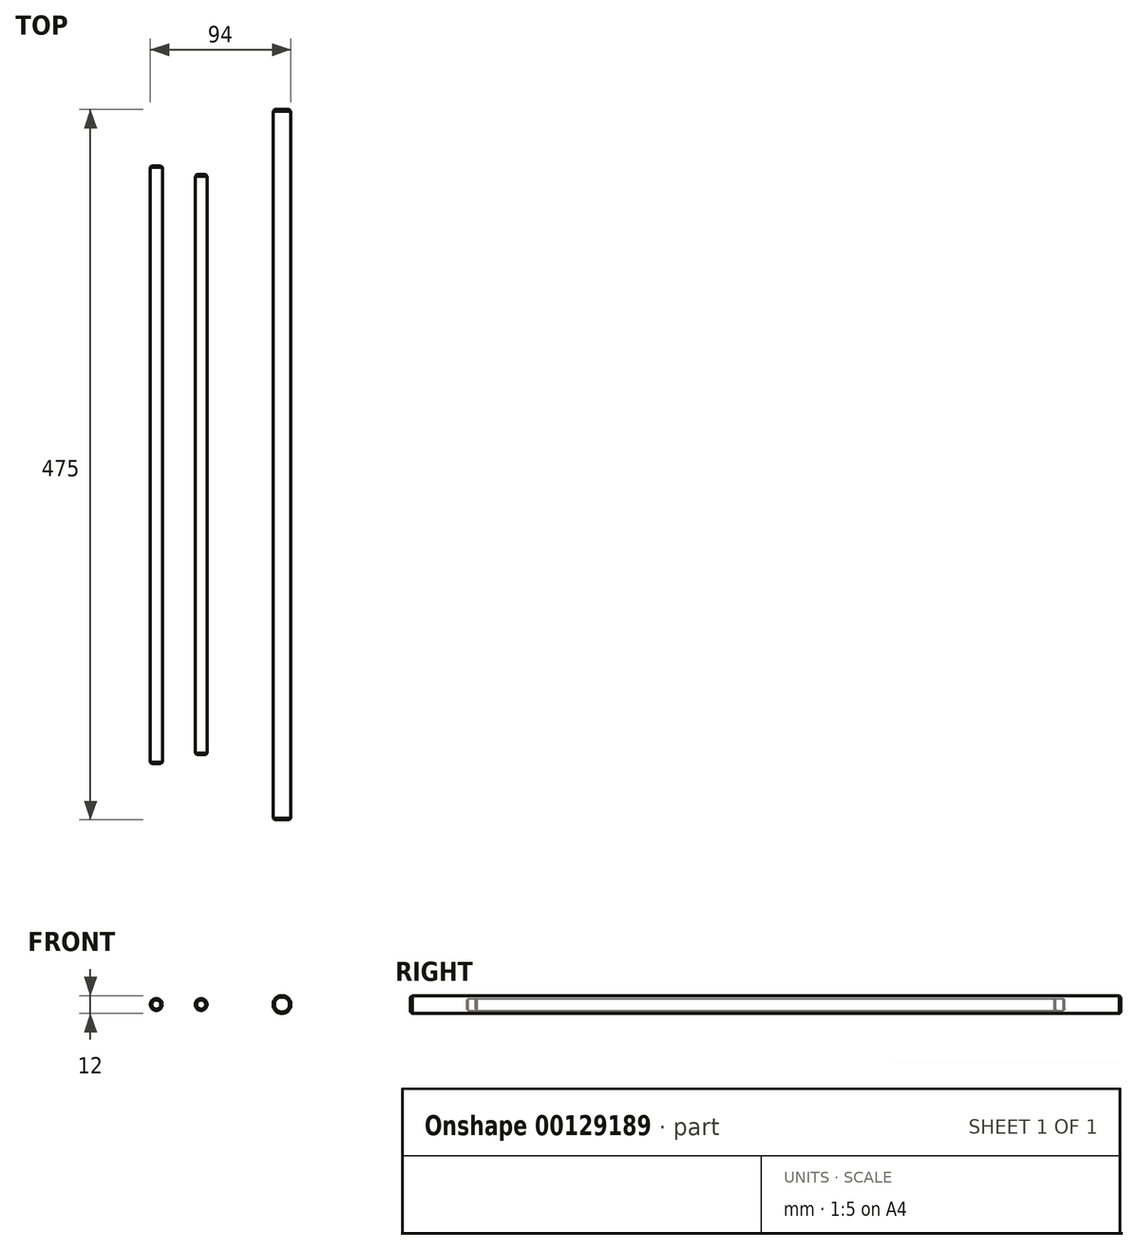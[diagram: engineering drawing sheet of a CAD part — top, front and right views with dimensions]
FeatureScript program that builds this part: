
annotation { "Feature Type Name" : "Feature", "Feature Type Description" : "" }
export const myFeature = defineFeature(function(context is Context, id is Id, definition is map)
    precondition{}
    {
        {
            assignVariable(context, id + "F0", {"name" : "Comprimento_Veio_X", "anyValue" : 388});
        }
        {
            assignVariable(context, id + "F1", {"name" : "Comprimento_Veio_Y", "anyValue" : 475});
        }
        {
            assignVariable(context, id + "F2", {"name" : "Comprimento_Veio_Z", "anyValue" : 400});
        }
        {
            var Q0;
            Q0=qCreatedBy(makeId("Front.planeOp"),FACE);
            var sketch = newSketch(context, id + "F3", { "sketchPlane" : qUnion([Q0])});
            skCircle(sketch, "E0", {"center": v(-30, 0) * mm, "radius": 4 * mm});
            skSolve(sketch);
        }
        {
            var Q0;
            Q0=makeQuery(id+"F3.imprint","IMPRINT",FACE,{"disambiguationData":[TD([[makeQuery(id+"F3.imprint","IMPRINT",EDGE,{"derivedFrom":sQuery(id+"F3.wireOp",EDGE,"E0")}),1.0]])]});
            extrude(context, id + "F4", {"entities" : qUnion([Q0]), "endBound" : BoundingType.SYMMETRIC, "depth" : (getVariable(context, 'Comprimento_Veio_X')) * mm});
        }
        {
            var Q0;
            Q0=makeQuery(id+"F4.opExtrude","CAP_EDGE",EDGE,{"disambiguationData":[OSD([sQuery(id+"F3.wireOp",EDGE,"E0")])],"isStart":false});
            var Q1;
            Q1=makeQuery(id+"F4.opExtrude","CAP_EDGE",EDGE,{"disambiguationData":[OSD([sQuery(id+"F3.wireOp",EDGE,"E0")])],"isStart":true});
            chamfer(context, id + "F5", {"entities" : qUnion([Q0, Q1]), "width" : 1 * mm, "tangentPropagation" : true});
        }
        {
            var Q0;
            Q0=qCreatedBy(makeId("Front.planeOp"),FACE);
            var sketch = newSketch(context, id + "F6", { "sketchPlane" : qUnion([Q0])});
            skCircle(sketch, "E1", {"center": v(24, 0) * mm, "radius": 6 * mm});
            skSolve(sketch);
        }
        {
            var Q0;
            Q0=qSketchRegion(id+"F6",true);
            extrude(context, id + "F7", {"entities" : qUnion([Q0]), "endBound" : BoundingType.SYMMETRIC, "depth" : (getVariable(context, 'Comprimento_Veio_Y')) * mm});
        }
        {
            var Q0;
            Q0=makeQuery(id+"F7.opExtrude","CAP_EDGE",EDGE,{"disambiguationData":[OSD([sQuery(id+"F6.wireOp",EDGE,"E1")])],"isStart":false});
            var Q1;
            Q1=makeQuery(id+"F7.opExtrude","CAP_EDGE",EDGE,{"disambiguationData":[OSD([sQuery(id+"F6.wireOp",EDGE,"E1")])],"isStart":true});
            chamfer(context, id + "F8", {"entities" : qUnion([Q0, Q1]), "width" : 1 * mm, "tangentPropagation" : true});
        }
        {
            var Q0;
            Q0=qCreatedBy(makeId("Front.planeOp"),FACE);
            var sketch = newSketch(context, id + "F9", { "sketchPlane" : qUnion([Q0])});
            skCircle(sketch, "E2", {"center": v(-60, 0) * mm, "radius": 4 * mm});
            skSolve(sketch);
        }
        {
            var Q0;
            Q0=makeQuery(id+"F9.imprint","IMPRINT",FACE,{"disambiguationData":[TD([[makeQuery(id+"F9.imprint","IMPRINT",EDGE,{"derivedFrom":sQuery(id+"F9.wireOp",EDGE,"E2")}),1.0]])]});
            extrude(context, id + "F10", {"entities" : qUnion([Q0]), "endBound" : BoundingType.SYMMETRIC, "depth" : (getVariable(context, 'Comprimento_Veio_Z')) * mm});
        }
        {
            var Q0;
            Q0=makeQuery(id+"F10.opExtrude","CAP_EDGE",EDGE,{"disambiguationData":[OSD([sQuery(id+"F9.wireOp",EDGE,"E2")])],"isStart":true});
            var Q1;
            Q1=makeQuery(id+"F10.opExtrude","CAP_EDGE",EDGE,{"disambiguationData":[OSD([sQuery(id+"F9.wireOp",EDGE,"E2")])],"isStart":false});
            chamfer(context, id + "F11", {"entities" : qUnion([Q0, Q1]), "width" : 1 * mm, "tangentPropagation" : true});
        }
    });
